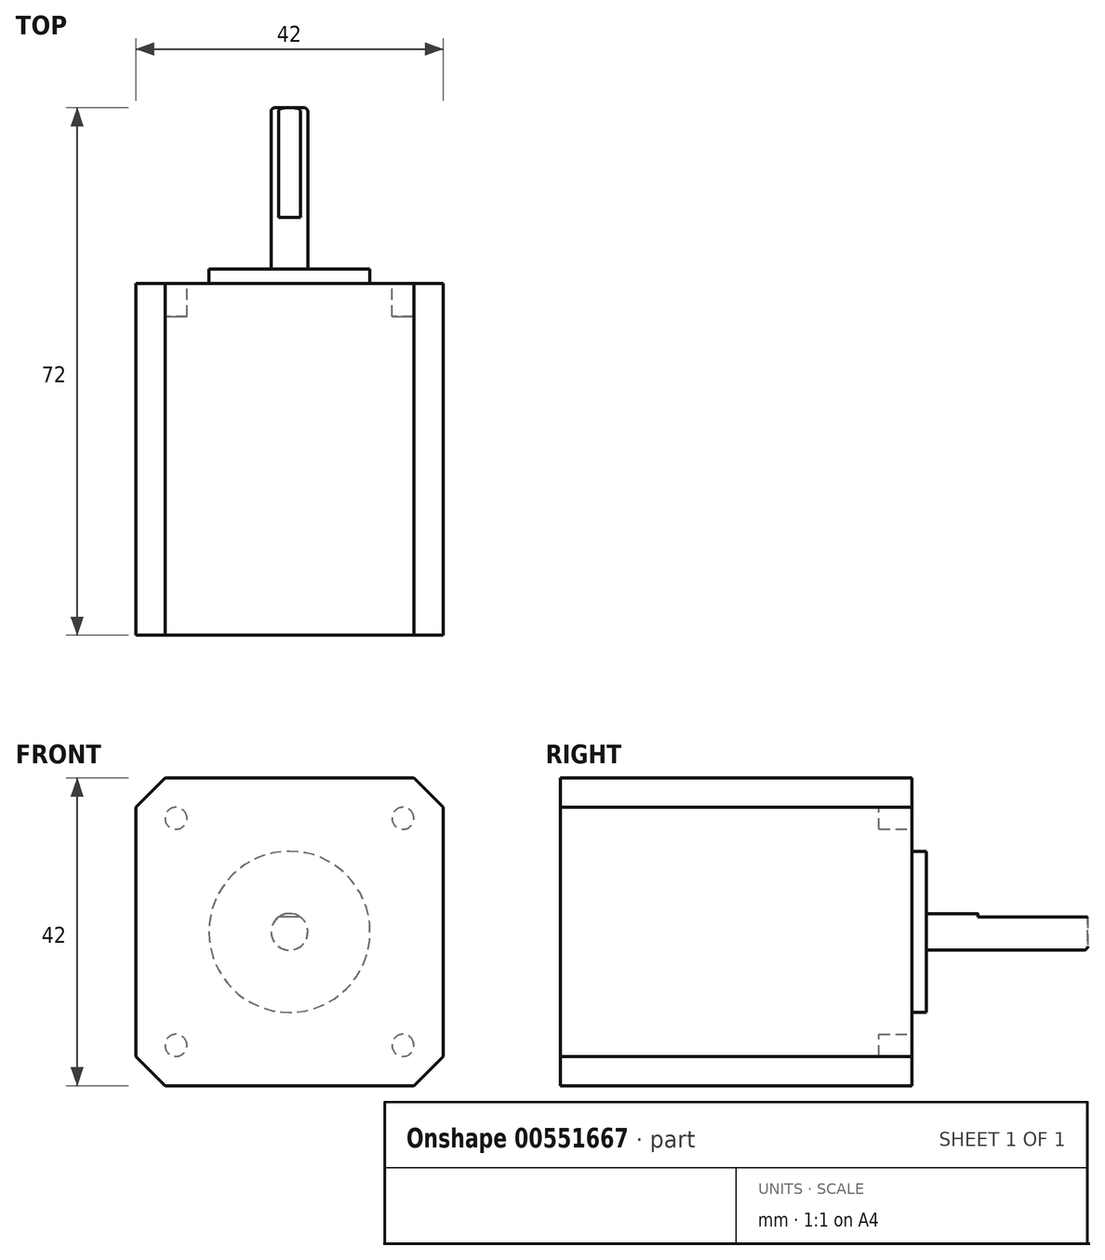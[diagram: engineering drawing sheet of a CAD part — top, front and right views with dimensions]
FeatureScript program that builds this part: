
annotation { "Feature Type Name" : "Feature", "Feature Type Description" : "" }
export const myFeature = defineFeature(function(context is Context, id is Id, definition is map)
    precondition{}
    {
        {
            var Q0;
            Q0=qCreatedBy(makeId("Front.planeOp"),FACE);
            var sketch = newSketch(context, id + "F0", { "sketchPlane" : qUnion([Q0])});
            skLineSegment(sketch, "E0.bottom", {"start": v(21, -21) * mm, "end": v(-21, -21) * mm});
            skLineSegment(sketch, "E0.top", {"start": v(21, 21) * mm, "end": v(-21, 21) * mm});
            skLineSegment(sketch, "E0.left", {"start": v(21, -21) * mm, "end": v(21, 21) * mm});
            skLineSegment(sketch, "E0.right", {"start": v(-21, -21) * mm, "end": v(-21, 21) * mm});
            skPoint(sketch, "E0.middle", {"position": v(0, 0) * mm});
            skLineSegment(sketch, "E1", {"start": v(-21, 17) * mm, "end": v(-17, 21) * mm});
            skLineSegment(sketch, "E2", {"start": v(17, 21) * mm, "end": v(21, 17) * mm});
            skLineSegment(sketch, "E3", {"start": v(-21, -17) * mm, "end": v(-17, -21) * mm});
            skCircle(sketch, "E4", {"center": v(-15.5, 15.5) * mm, "radius": 1.5 * mm});
            skCircle(sketch, "E5", {"center": v(15.5, 15.5) * mm, "radius": 1.5 * mm});
            skCircle(sketch, "E6", {"center": v(-15.5, -15.5) * mm, "radius": 1.5 * mm});
            skCircle(sketch, "E7", {"center": v(15.5, -15.5) * mm, "radius": 1.5 * mm});
            skLineSegment(sketch, "E8.bottom", {"start": v(15.5, -15.5) * mm, "end": v(-15.5, -15.5) * mm, "construction": true});
            skLineSegment(sketch, "E8.top", {"start": v(15.5, 15.5) * mm, "end": v(-15.5, 15.5) * mm, "construction": true});
            skLineSegment(sketch, "E8.left", {"start": v(15.5, -15.5) * mm, "end": v(15.5, 15.5) * mm, "construction": true});
            skLineSegment(sketch, "E8.right", {"start": v(-15.5, -15.5) * mm, "end": v(-15.5, 15.5) * mm, "construction": true});
            skLineSegment(sketch, "E9", {"start": v(17, 15.5) * mm, "end": v(17, 21) * mm, "construction": true});
            skLineSegment(sketch, "E10", {"start": v(15.35, 17) * mm, "end": v(21, 17) * mm, "construction": true});
            skLineSegment(sketch, "E11", {"start": v(15.5, -17) * mm, "end": v(21, -17) * mm, "construction": true});
            skLineSegment(sketch, "E12", {"start": v(17, -15.5) * mm, "end": v(17, -21) * mm, "construction": true});
            skLineSegment(sketch, "E13", {"start": v(-17, -15.5) * mm, "end": v(-17, -21) * mm, "construction": true});
            skLineSegment(sketch, "E14", {"start": v(-15.5, -17) * mm, "end": v(-21, -17) * mm, "construction": true});
            skLineSegment(sketch, "E15", {"start": v(-17, 15.5) * mm, "end": v(-17, 21) * mm, "construction": true});
            skLineSegment(sketch, "E16", {"start": v(-15.5, 17) * mm, "end": v(-21, 17) * mm, "construction": true});
            skLineSegment(sketch, "E17", {"start": v(17, -21) * mm, "end": v(21, -17) * mm});
            skSolve(sketch);
        }
        {
            var Q0;
            {var subQ2=sQuery(id+"F0.wireOp",EDGE,"E1");Q0=makeQuery(id+"F0.imprint","IMPRINT",FACE,{"disambiguationData":[TD([[makeQuery(id+"F0.imprint","IMPRINT",EDGE,{"derivedFrom":subQ2}),-1.0]])]});}
            var Q1;
            Q1=makeQuery(id+"F0.imprint","IMPRINT",FACE,{"disambiguationData":[TD([[makeQuery(id+"F0.imprint","IMPRINT",EDGE,{"derivedFrom":sQuery(id+"F0.wireOp",EDGE,"E4")}),1.0]])]});
            var Q2;
            Q2=makeQuery(id+"F0.imprint","IMPRINT",FACE,{"disambiguationData":[TD([[makeQuery(id+"F0.imprint","IMPRINT",EDGE,{"derivedFrom":sQuery(id+"F0.wireOp",EDGE,"E5")}),1.0]])]});
            var Q3;
            Q3=makeQuery(id+"F0.imprint","IMPRINT",FACE,{"disambiguationData":[TD([[makeQuery(id+"F0.imprint","IMPRINT",EDGE,{"derivedFrom":sQuery(id+"F0.wireOp",EDGE,"E6")}),1.0]])]});
            var Q4;
            Q4=makeQuery(id+"F0.imprint","IMPRINT",FACE,{"disambiguationData":[TD([[makeQuery(id+"F0.imprint","IMPRINT",EDGE,{"derivedFrom":sQuery(id+"F0.wireOp",EDGE,"E7")}),1.0]])]});
            extrude(context, id + "F1", {"entities" : qUnion([Q0, Q1, Q2, Q3, Q4]), "depth" : 48 * mm, "offsetDistance" : 25 * mm});
        }
        {
            var Q0;
            Q0=makeQuery(id+"F0.imprint","IMPRINT",FACE,{"disambiguationData":[TD([[makeQuery(id+"F0.imprint","IMPRINT",EDGE,{"derivedFrom":sQuery(id+"F0.wireOp",EDGE,"E4")}),1.0]])]});
            var Q1;
            Q1=makeQuery(id+"F0.imprint","IMPRINT",FACE,{"disambiguationData":[TD([[makeQuery(id+"F0.imprint","IMPRINT",EDGE,{"derivedFrom":sQuery(id+"F0.wireOp",EDGE,"E6")}),1.0]])]});
            var Q2;
            Q2=makeQuery(id+"F0.imprint","IMPRINT",FACE,{"disambiguationData":[TD([[makeQuery(id+"F0.imprint","IMPRINT",EDGE,{"derivedFrom":sQuery(id+"F0.wireOp",EDGE,"E5")}),1.0]])]});
            var Q3;
            Q3=makeQuery(id+"F0.imprint","IMPRINT",FACE,{"disambiguationData":[TD([[makeQuery(id+"F0.imprint","IMPRINT",EDGE,{"derivedFrom":sQuery(id+"F0.wireOp",EDGE,"E7")}),1.0]])]});
            extrude(context, id + "F2", {"entities" : qUnion([Q0, Q1, Q2, Q3]), "operationType" : NewBodyOperationType.REMOVE, "depth" : 4.5 * mm, "offsetDistance" : 25 * mm});
        }
        {
            var Q0;
            {var subQ2=sQuery(id+"F0.wireOp",EDGE,"E1");Q0=makeQuery(id+"F0.imprint","IMPRINT",FACE,{"disambiguationData":[TD([[makeQuery(id+"F0.imprint","IMPRINT",EDGE,{"derivedFrom":subQ2}),-1.0]])]});}
            var sketch = newSketch(context, id + "F3", { "sketchPlane" : qUnion([Q0])});
            skCircle(sketch, "E18", {"center": v(0, 0) * mm, "radius": 11 * mm});
            skSolve(sketch);
        }
        {
            var Q0;
            Q0=qSketchRegion(id+"F3",true);
            extrude(context, id + "F4", {"entities" : qUnion([Q0]), "operationType" : NewBodyOperationType.ADD, "oppositeDirection" : true, "depth" : 2 * mm, "offsetDistance" : 25 * mm});
        }
        {
            var Q0;
            Q0=makeQuery(id+"F4.opExtrude","CAP_FACE",FACE,{"disambiguationData":[OSD([sQuery(id+"F3.wireOp",EDGE,"E18")])],"isStart":false});
            var sketch = newSketch(context, id + "F5", { "sketchPlane" : qUnion([Q0])});
            skCircle(sketch, "E19", {"center": v(0, 0) * mm, "radius": 2.5 * mm});
            skSolve(sketch);
        }
        {
            var Q0;
            Q0=qSketchRegion(id+"F5",true);
            extrude(context, id + "F6", {"entities" : qUnion([Q0]), "depth" : 22 * mm, "offsetDistance" : 25 * mm});
        }
        {
            var Q0;
            Q0=makeQuery(id+"F6.opExtrude","CAP_FACE",FACE,{"disambiguationData":[OSD([sQuery(id+"F5.wireOp",EDGE,"E19")])],"isStart":false});
            var sketch = newSketch(context, id + "F7", { "sketchPlane" : qUnion([Q0])});
            skLineSegment(sketch, "E20", {"start": v(-1.5, 2) * mm, "end": v(1.5, 2) * mm});
            skSolve(sketch);
        }
        {
            var Q0;
            Q0=qSketchRegion(id+"F7",true);
            var Q1;
            {var subQ0=sQuery(id+"F7.wireOp",EDGE,"E20");Q1=makeQuery(id+"F7.imprint","IMPRINT",FACE,{"disambiguationData":[TD([[makeQuery(id+"F7.imprint","IMPRINT",EDGE,{"derivedFrom":subQ0}),1.0]])]});}
            extrude(context, id + "F8", {"entities" : qUnion([Q0, Q1]), "operationType" : NewBodyOperationType.REMOVE, "oppositeDirection" : true, "depth" : 15 * mm, "offsetDistance" : 25 * mm});
        }
        {
            var Q0;
            Q0=makeQuery(id+"F6.opExtrude","CAP_EDGE",EDGE,{"disambiguationData":[OSD([sQuery(id+"F5.wireOp",EDGE,"E19")])],"isStart":false});
            fillet(context, id + "F9", {"entities" : qUnion([Q0]), "radius" : .5 * mm, "tangentPropagation" : true, "allowEdgeOverflow" : false});
        }
    });
